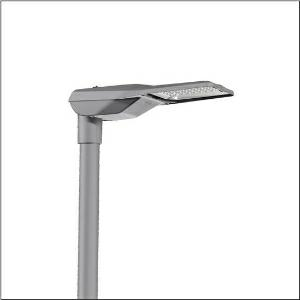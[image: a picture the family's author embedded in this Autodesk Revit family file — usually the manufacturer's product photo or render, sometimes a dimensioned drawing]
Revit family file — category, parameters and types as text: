
# Revit family: streetlight_sl_21_mini___st0_8a_5xe2c33s08jb_c287
name_source: partatom
category: Lighting Fixtures
units: mm (PartAtom-declared; Revit-internal decimal feet)

## family parameters
Cut with Voids When Loaded = No
Host = Face
Light Source = No
Part Type = Normal
Room Calculation Point = No
Round Connector Dimension = Use Diameter
Shared = No

## types (1)
- --- (1 x LED, 12940 lm, 88.6 W, 3000K)
    Apparent Load = 89 VA
    CIE Flux Codes = 41 75 97 100 100
    Color Rendering = 70
    Color Temperature = 3000K
    Default Elevation = 1800 mm
    Description = Streetlight SL 21 mini, mast luminaire, primary light control with lens, of PMMA, primary optical cover: cover, of toughened safety glass, transparent, light distribution: ST0.8a, light emission: direct distribution, primary light characteristic: asymmetric, installation type: side-entry, post-top, LED, High Power LED, rated luminous flux: 12.940lm, luminous efficacy: 146lm/W, light colour: 730, colour temperature: 3000K, control gear: D4i, control: overheat protection, constant luminous flux control, time-dependent luminous flux control, flexible luminous flux parameterisation, pre-setting: logarithmic dimming characteristic, mains connection: 220..240V, AC, 50/60Hz, start of lifetime: 89W, end of service life: 92W, reduction: 41W, luminaire housing, of diecast aluminium, powder-coated, SITECO metallic grey (DB 702S), corrosivity category C5 high according to DIN EN ISO 12944, please order mast flange separately, inclination adjustable: 0°, 5°, 10°, 15°, sealing non-destructively replaceable, multi-level sealing system, length: 628mm, width: 235mm, height: 110mm, mast flange for spigot size: 42mm (side-entry): 5XC10008XM4, 60/48mm (side-entry/post-top): 5XC10108XM2, 76/60mm (side-entry/post-top): 5XC10108XM1, mounting height: 4..8m, Smart Interface above, protection rating (complete): IP66, insulation class (complete): insulation class II (safety insulation), certification: CE, ENEC, ENEC+, VDE, impact resistance: IK10, permissible operating ambient temperature for outdoor applications: -40..+50°C, standard-compliant lighting for roads and squares, packaging unit: 1 piece

Light Distribution: ST0.8a
    Height = 110 mm
    Lamp = 1 x LED
    Lamp Light Flux = 12940 lm
    Lamp Power = 88.6 W
    Lamp count = 1
    Length = 625 mm
    Luminous efficacy = 146 lm/W
    Manufacturer = Siteco
    ModVariant = No
    Model = 5XE2C33S08JB
    Number of Poles = 1
    OnlyDefault = Yes
    Power Factor = 1
    Product Name = Streetlight SL 21 mini | ST0.8a
    Product group = mast luminaire | pylon top
    ProductGroupID = 6100
    Protection Class = Protection class II
    Protection Degree = IP 66
    RLX_Detail_Level = 1
    RLX_Emergency_Light_Flux = 0 lm
    RLX_Emergency_Type = 0
    RLX_Emergency_Type_DB = No
    RlxData = <blob elided: 26209 chars, md5=8c67b3fa>
    Socket = socket
    Standby Power = 0 W
    System Light Flux = 12940 lm
    System Power = 89 W
    Type Comments = factory setting: luminous flux: 100 % | dim-lin: 254 | 915 mA
    Type Image = l_1003515.jpg
    URL = http://relux.com
    VarID = @adj_030741
    Voltage = 0 V
    Weight = 0.00 kg
    Width = 234 mm

## geometry (parser evidence)
native form markers: Blend x4, Sweep x12
no freeform markers — native parametric forms only
